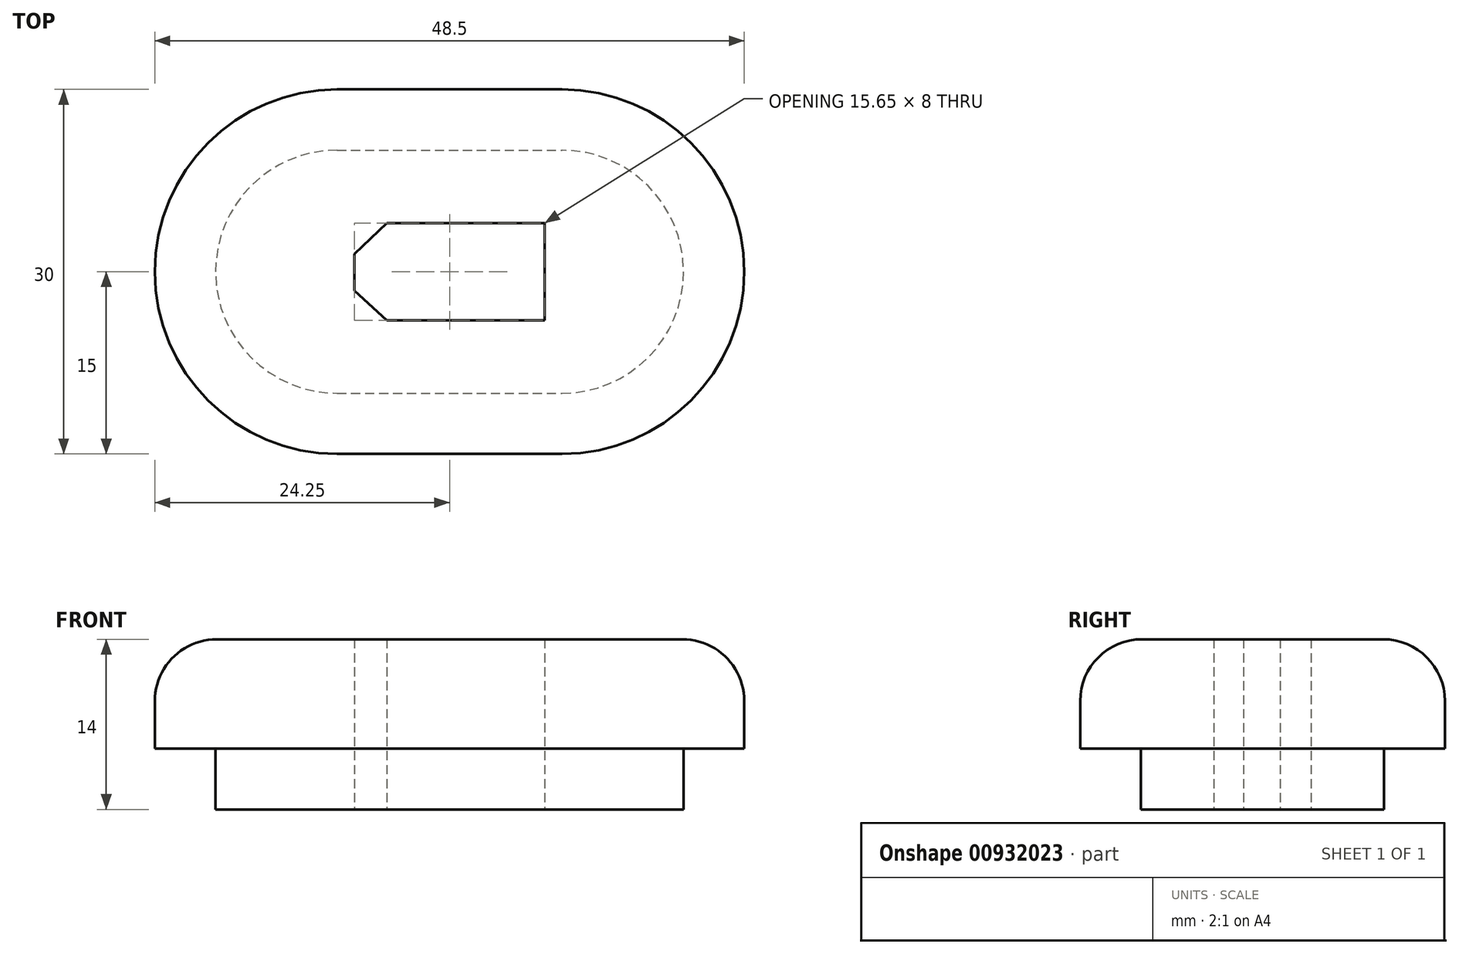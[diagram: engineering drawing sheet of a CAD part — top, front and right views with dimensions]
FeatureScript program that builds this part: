
annotation { "Feature Type Name" : "Feature", "Feature Type Description" : "" }
export const myFeature = defineFeature(function(context is Context, id is Id, definition is map)
    precondition{}
    {
        {
            var Q0;
            Q0=qCreatedBy(makeId("Top.planeOp"),FACE);
            var sketch = newSketch(context, id + "F0", { "sketchPlane" : qUnion([Q0])});
            skArc(sketch, "E0", {"start": v(-31.44, 10) * mm, "mid": v(-41.44, 0) * mm, "end": v(-31.44, -10) * mm});
            skArc(sketch, "E1", {"start": v(-12.94, -10) * mm, "mid": v(-2.94, 0) * mm, "end": v(-12.94, 10) * mm});
            skLineSegment(sketch, "E2", {"start": v(-31.44, 10) * mm, "end": v(-12.94, 10) * mm});
            skLineSegment(sketch, "E3", {"start": v(-31.44, -10) * mm, "end": v(-12.94, -10) * mm});
            skLineSegment(sketch, "E4", {"start": v(-22.19, 10) * mm, "end": v(-22.19, -10) * mm});
            skLineSegment(sketch, "E5", {"start": v(-41.44, 0) * mm, "end": v(-2.94, 0) * mm});
            skLineSegment(sketch, "E6.bottom", {"start": v(-14.36, -4) * mm, "end": v(-27.36, -4) * mm});
            skLineSegment(sketch, "E6.top", {"start": v(-14.36, 4) * mm, "end": v(-27.36, 4) * mm});
            skLineSegment(sketch, "E6.left", {"start": v(-14.36, -4) * mm, "end": v(-14.36, 4) * mm});
            skLineSegment(sketch, "E6.right", {"start": v(-30.01, -1.56) * mm, "end": v(-30.01, 1.44) * mm});
            skPoint(sketch, "E6.middle", {"position": v(-22.19, 0) * mm});
            skPoint(sketch, "E7", {"position": v(-27.36, -4) * mm});
            skPoint(sketch, "E8", {"position": v(-27.36, 4) * mm});
            skLineSegment(sketch, "E9", {"start": v(-27.36, -4) * mm, "end": v(-30.01, -1.56) * mm});
            skLineSegment(sketch, "E10", {"start": v(-30.01, 1.44) * mm, "end": v(-27.36, 4) * mm});
            skSolve(sketch);
        }
        {
            var Q0;
            Q0 = qSketchRegion(id + "F0", true);
            extrude(context, id + "F1", {"entities" : qUnion([Q0]), "depth" : 14 * mm, "offsetDistance" : 25.4 * mm});
        }
        {
            var Q0;
            Q0=qCreatedBy(makeId("Top.planeOp"),FACE);
            cPlane(context, id + "F2", {"entities" : qUnion([Q0]), "cplaneType" : CPlaneType.OFFSET, "offset" : 14 * mm, "width" : 152.4 * mm, "height" : 152.4 * mm});
        }
        {
            var Q0;
            Q0=qCreatedBy(id+"F2.planeOp",FACE);
            var sketch = newSketch(context, id + "F3", { "sketchPlane" : qUnion([Q0])});
            skArc(sketch, "E11", {"start": v(-31.44, 15) * mm, "mid": v(-46.44, 0) * mm, "end": v(-31.44, -15) * mm});
            skArc(sketch, "E12", {"start": v(-12.94, -15) * mm, "mid": v(2.06, 0) * mm, "end": v(-12.94, 15) * mm});
            skLineSegment(sketch, "E13", {"start": v(-31.44, 15) * mm, "end": v(-12.94, 15) * mm});
            skLineSegment(sketch, "E14", {"start": v(-31.44, -15) * mm, "end": v(-12.94, -15) * mm});
            skSolve(sketch);
        }
        {
            var Q0;
            Q0 = qSketchRegion(id + "F3", true);
            extrude(context, id + "F4", {"entities" : qUnion([Q0]), "operationType" : NewBodyOperationType.ADD, "oppositeDirection" : true, "depth" : 9 * mm, "offsetDistance" : 25.4 * mm});
        }
        {
            var Q0;
            Q0=makeQuery(id+"F4.boolean.opBoolean","SPLIT",FACE,{"disambiguationData":[TD([makeQuery(id+"F1.opExtrude","SWEPT_FACE",FACE,{"disambiguationData":[OSD([sQuery(id+"F0.wireOp",EDGE,"E6.bottom")])]})])],"derivedFrom":makeQuery(id+"F4.opExtrude","CAP_FACE",FACE,{"disambiguationData":[OSD([sQuery(id+"F3.wireOp",EDGE,"E11"),sQuery(id+"F3.wireOp",EDGE,"E12"),sQuery(id+"F3.wireOp",EDGE,"E13"),sQuery(id+"F3.wireOp",EDGE,"E14")])],"isStart":false})});
            extrude(context, id + "F5", {"entities" : qUnion([Q0]), "operationType" : NewBodyOperationType.REMOVE, "oppositeDirection" : true, "depth" : 25.4 * mm, "offsetDistance" : 25.4 * mm});
        }
        {
            var Q0;
            Q0=makeQuery(id+"F4.opExtrude","CAP_EDGE",EDGE,{"disambiguationData":[OSD([sQuery(id+"F3.wireOp",EDGE,"E14")])],"isStart":true});
            fillet(context, id + "F6", {"entities" : qUnion([Q0]), "radius" : 5.08 * mm, "tangentPropagation" : true, "allowEdgeOverflow" : false});
        }
    });
